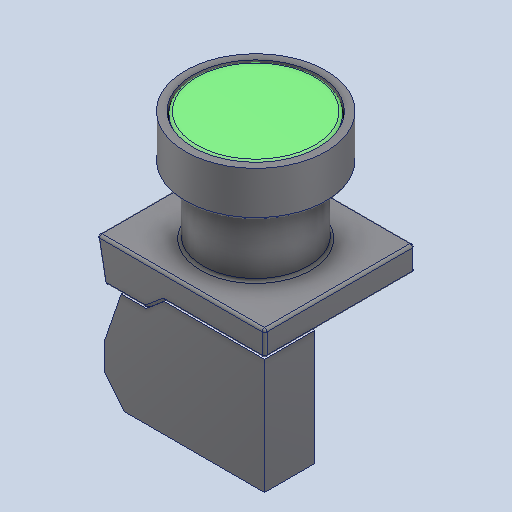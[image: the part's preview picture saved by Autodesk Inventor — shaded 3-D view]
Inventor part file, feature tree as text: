
AUTODESK INVENTOR PART (.ipt)
format: ipt  version: 2025.2 (Build 292293000, 293)  size: 206,336 bytes
history: native  units: mm
features: other x1, fillet x1
ambient origin geometry x8: Origin, YZ Plane, XZ Plane, XY Plane, X Axis, Y Axis, Z Axis, Center Point
bodies: Solid1 (feature_tree), Solid2 (feature_tree)
feature tree (2):
  other  "Boss-Extrude1"
  fillet  "Fillet2"  [1 undecoded]
note: 1 required parameter value undecoded (feature->parameter linkage not recoverable at this tier; creation-order binding heuristic only, values carry confidence <= 0.55)
